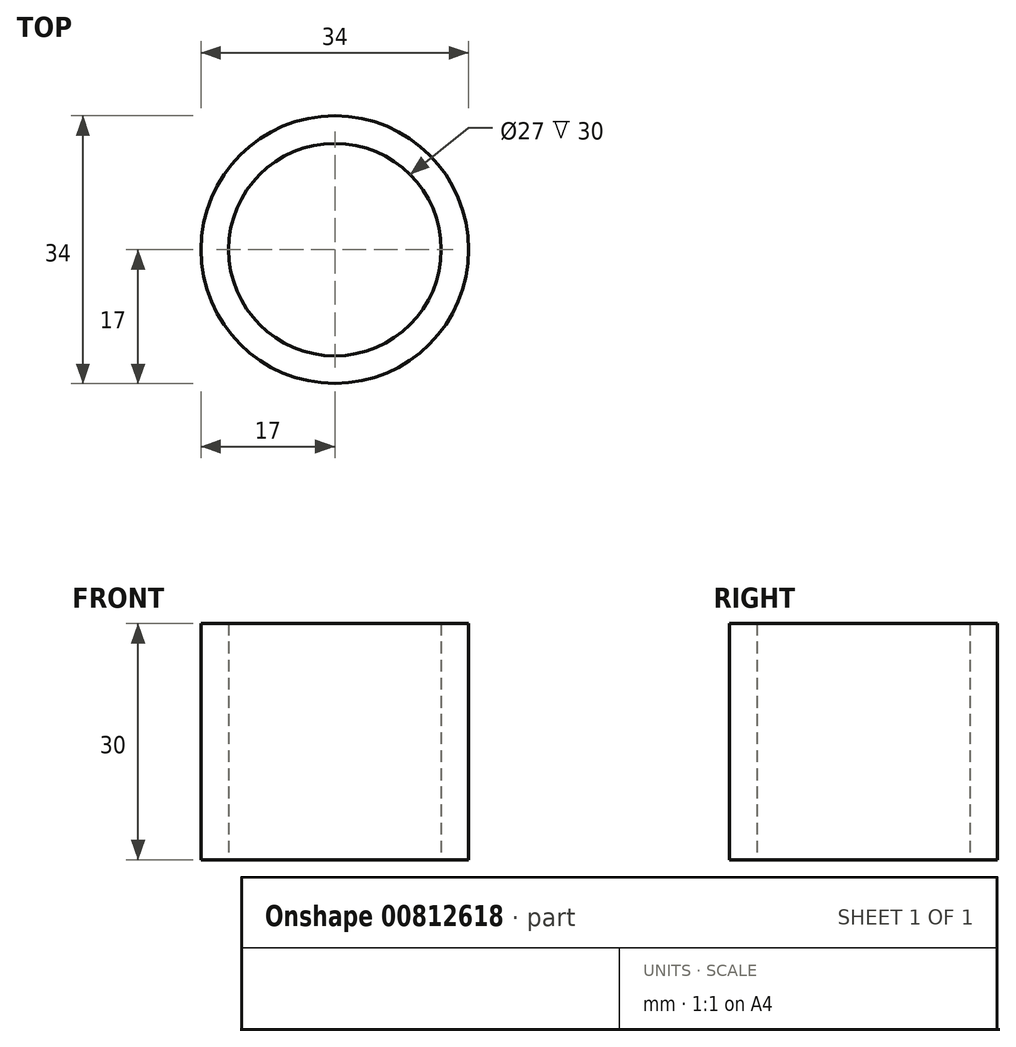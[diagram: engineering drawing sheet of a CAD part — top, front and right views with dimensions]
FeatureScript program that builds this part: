
annotation { "Feature Type Name" : "Feature", "Feature Type Description" : "" }
export const myFeature = defineFeature(function(context is Context, id is Id, definition is map)
    precondition{}
    {
        {
            var Q0;
            Q0=qCreatedBy(makeId("Top.planeOp"),FACE);
            var sketch = newSketch(context, id + "F0", { "sketchPlane" : qUnion([Q0])});
            skCircle(sketch, "E0", {"center": v(0, 0) * mm, "radius": 13.5 * mm});
            skCircle(sketch, "E1", {"center": v(0, 0) * mm, "radius": 17 * mm});
            skSolve(sketch);
        }
        {
            var Q0;
            Q0 = qSketchRegion(id + "F0", true);
            extrude(context, id + "F1", {"entities" : qUnion([Q0]), "depth" : 30 * mm, "offsetDistance" : 25 * mm});
        }
    });
